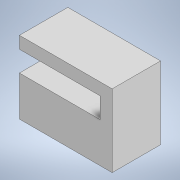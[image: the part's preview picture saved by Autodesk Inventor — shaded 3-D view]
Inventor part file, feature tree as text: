
AUTODESK INVENTOR PART (.ipt)
format: ipt  version: 2020 (Build 240168000, 168)  size: 101,888 bytes
history: native  units: mm
features: extrude x2, imported_body x1, sketch x1
ambient origin geometry x8: Origin, YZ Plane, XZ Plane, XY Plane, X Axis, Y Axis, Z Axis, Center Point
bodies: Solid1 (feature_tree)
feature tree (4):
  extrude  "Extrusion1"  Depth=12.0mm
  extrude  "Extrusion3"  Depth=18.0mm TaperAngle=0.0deg
  imported_body  "base"
  sketch  "Sketch3"  dims[d0=23.0mm d1=12.0mm d2=18.0mm d3=0.0mm d9=5.1mm d10=3.0mm d11=3.0mm d12=9.0mm d13=0.0mm]
